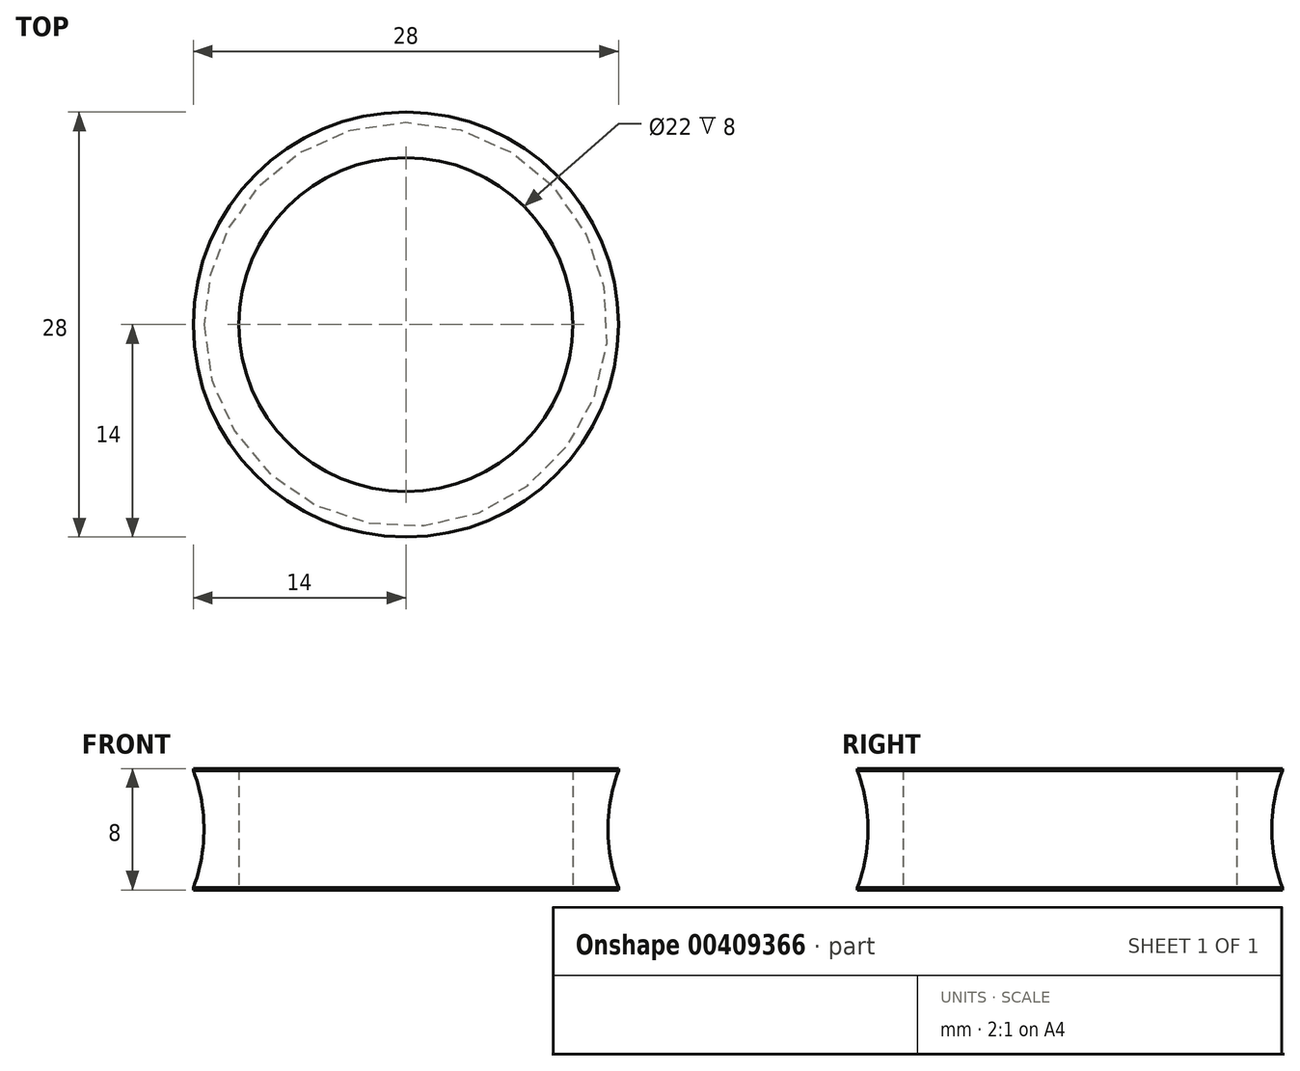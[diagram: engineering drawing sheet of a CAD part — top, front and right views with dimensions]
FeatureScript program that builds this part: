
annotation { "Feature Type Name" : "Feature", "Feature Type Description" : "" }
export const myFeature = defineFeature(function(context is Context, id is Id, definition is map)
    precondition{}
    {
        {
            var Q0;
            Q0=qCreatedBy(makeId("Front.planeOp"),FACE);
            var sketch = newSketch(context, id + "F0", { "sketchPlane" : qUnion([Q0])});
            skLineSegment(sketch, "E0.bottom", {"start": v(11, 0) * mm, "end": v(14, 0) * mm});
            skLineSegment(sketch, "E0.top", {"start": v(11, 8) * mm, "end": v(14, 8) * mm});
            skLineSegment(sketch, "E0.left", {"start": v(11, 0) * mm, "end": v(11, 8) * mm});
            skLineSegment(sketch, "E0.right", {"start": v(14, 0) * mm, "end": v(14, 0.14) * mm});
            skArc(sketch, "E1", {"start": v(14, 7.86) * mm, "mid": v(13.3, 4) * mm, "end": v(14, 0.14) * mm});
            skLineSegment(sketch, "E2", {"start": v(14, 4) * mm, "end": v(34.6, 4) * mm, "construction": true});
            skLineSegment(sketch, "E3.trimOffspring", {"start": v(14, 7.86) * mm, "end": v(14, 8) * mm});
            skLineSegment(sketch, "E4", {"start": v(0, 0) * mm, "end": v(0, 16.99) * mm});
            skSolve(sketch);
        }
        {
            var Q0;
            Q0=makeQuery(id+"F0.imprint","IMPRINT",FACE,{"disambiguationData":[TD([[makeQuery(id+"F0.imprint","IMPRINT",EDGE,{"derivedFrom":sQuery(id+"F0.wireOp",EDGE,"E0.bottom")}),1.0]])]});
            var Q1;
            Q1=sQuery(id+"F0.wireOp",EDGE,"E4");
            revolve(context, id + "F1", {"entities" : qUnion([Q0]), "axis" : qUnion([Q1]), "revolveType" : RevolveType.FULL});
        }
    });
